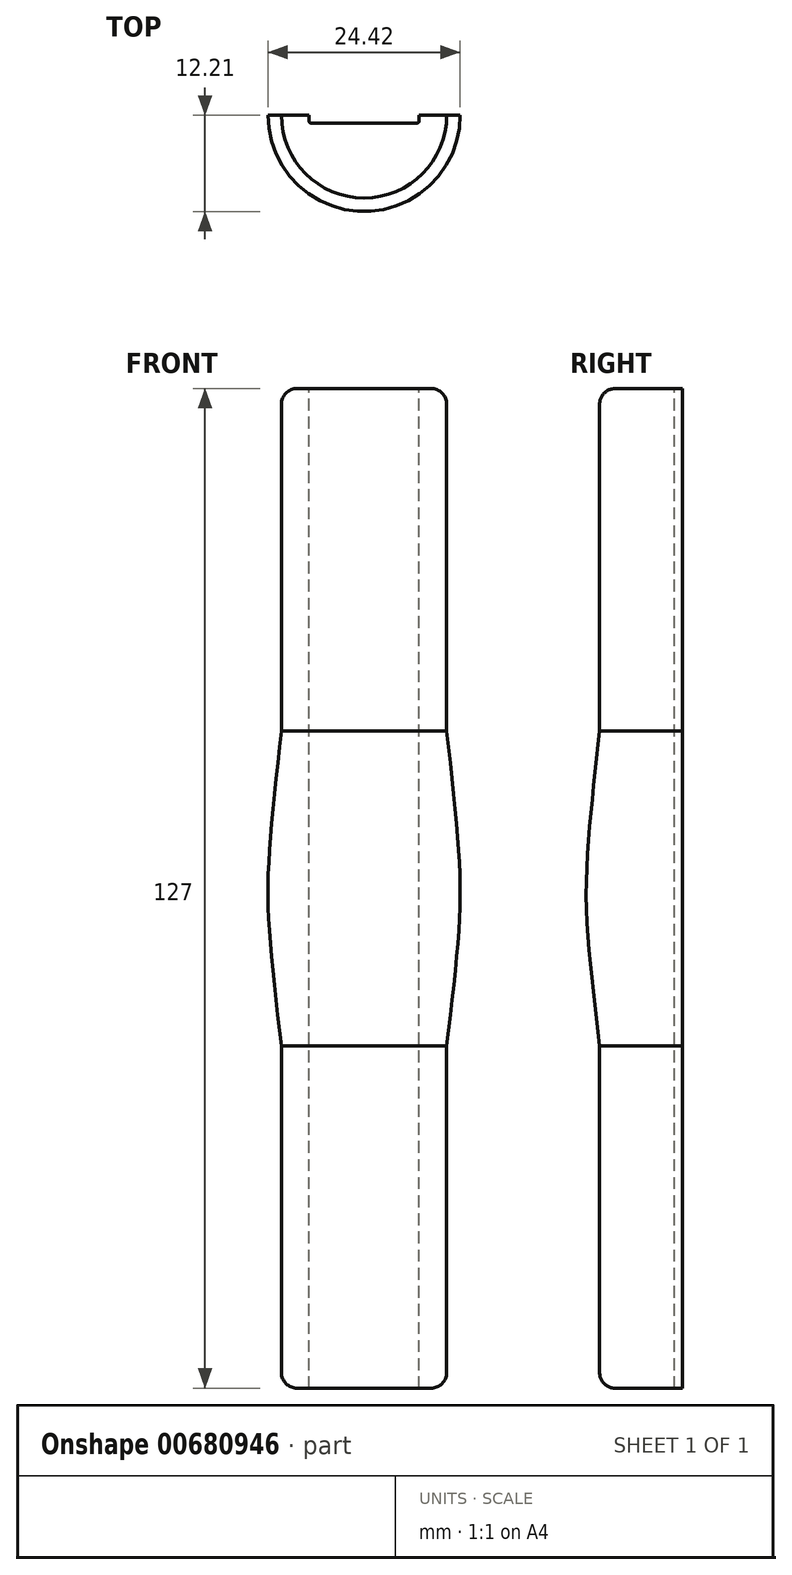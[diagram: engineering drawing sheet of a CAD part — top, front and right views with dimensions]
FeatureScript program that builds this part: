
annotation { "Feature Type Name" : "Feature", "Feature Type Description" : "" }
export const myFeature = defineFeature(function(context is Context, id is Id, definition is map)
    precondition{}
    {
        {
            var Q0;
            Q0=qCreatedBy(makeId("Front.planeOp"),FACE);
            var sketch = newSketch(context, id + "F0", { "sketchPlane" : qUnion([Q0])});
            skLineSegment(sketch, "E0.bottom", {"start": v(-5.25, 63.5) * mm, "end": v(5.25, 63.5) * mm});
            skLineSegment(sketch, "E0.top", {"start": v(-5.25, -63.5) * mm, "end": v(5.25, -63.5) * mm});
            skLineSegment(sketch, "E0.left", {"start": v(-5.25, 63.5) * mm, "end": v(-5.25, 20) * mm});
            skLineSegment(sketch, "E0.right", {"start": v(5.25, 63.5) * mm, "end": v(5.25, -63.5) * mm});
            skPoint(sketch, "E0.middle", {"position": v(0, 0) * mm});
            skFitSpline(sketch, "E1", {"points": [v(-5.25, 20) * mm, v(-6.8, 4.2) * mm, v(-6.8, -5.12) * mm, v(-5.25, -20) * mm], "startDerivative": vector(-5.22, -46.75) * mm, "endDerivative": vector(5.38, -45.13) * mm});
            skLineSegment(sketch, "E2.trimOffspring", {"start": v(-5.25, -20) * mm, "end": v(-5.25, -63.5) * mm});
            skPoint(sketch, "E3.orphan", {"position": v(-5.25, 0) * mm});
            skSolve(sketch);
        }
        {
            var Q0;
            Q0=makeQuery(id+"F0.imprint","IMPRINT",FACE,{"disambiguationData":[TD([[makeQuery(id+"F0.imprint","IMPRINT",EDGE,{"derivedFrom":sQuery(id+"F0.wireOp",EDGE,"E0.bottom")}),-1.0]])]});
            var Q1;
            Q1=sQuery(id+"F0.wireOp",EDGE,"E0.right");
            revolve(context, id + "F1", {"entities" : qUnion([Q0]), "axis" : qUnion([Q1]), "revolveType" : RevolveType.ONE_DIRECTION, "angle" : 180 * degree});
        }
        {
            var Q0;
            Q0=makeQuery(id+"F1.opRevolve","SWEPT_FACE",FACE,{"disambiguationData":[OSD([sQuery(id+"F0.wireOp",EDGE,"E0.bottom")])]});
            var sketch = newSketch(context, id + "F2", { "sketchPlane" : qUnion([Q0])});
            skLineSegment(sketch, "E4", {"start": v(5.25, 0) * mm, "end": v(-1.75, 0) * mm});
            skLineSegment(sketch, "E5", {"start": v(5.25, 0) * mm, "end": v(12.25, 0) * mm});
            skLineSegment(sketch, "E6", {"start": v(12.25, 0) * mm, "end": v(12.25, 0.7) * mm});
            skLineSegment(sketch, "E7", {"start": v(11.95, 1) * mm, "end": v(-1.45, 1) * mm});
            skLineSegment(sketch, "E8", {"start": v(-1.75, 0.7) * mm, "end": v(-1.75, 0) * mm});
            skPoint(sketch, "E9.visualSharp", {"position": v(-1.75, 1) * mm});
            skArc(sketch, "E9.filletArc", {"start": v(-1.45, 1) * mm, "mid": v(-1.66, 0.91) * mm, "end": v(-1.75, 0.7) * mm});
            skPoint(sketch, "E10.visualSharp", {"position": v(12.25, 1) * mm});
            skArc(sketch, "E10.filletArc", {"start": v(12.25, 0.7) * mm, "mid": v(12.16, 0.91) * mm, "end": v(11.95, 1) * mm});
            skSolve(sketch);
        }
        {
            var Q0;
            Q0=makeQuery(id+"F2.imprint","IMPRINT",FACE,{"disambiguationData":[TD([[makeQuery(id+"F2.imprint","IMPRINT",EDGE,{"derivedFrom":sQuery(id+"F2.wireOp",EDGE,"E4")}),-1.0]])]});
            extrude(context, id + "F3", {"entities" : qUnion([Q0]), "operationType" : NewBodyOperationType.REMOVE, "oppositeDirection" : true, "depth" : 127 * mm, "offsetDistance" : 25 * mm});
        }
        {
            var Q0;
            Q0=makeQuery(id+"F1.opRevolve","SWEPT_BODY",BODY,{"disambiguationData":[OSD([sQuery(id+"F0.wireOp",EDGE,"E0.bottom"),sQuery(id+"F0.wireOp",EDGE,"E0.top"),sQuery(id+"F0.wireOp",EDGE,"E0.right"),sQuery(id+"F0.wireOp",EDGE,"E0.left"),sQuery(id+"F0.wireOp",EDGE,"E1"),sQuery(id+"F0.wireOp",EDGE,"E2.trimOffspring")])]});
            var Q1;
            Q1=qCreatedBy(makeId("Front.planeOp"),FACE);
            mirror(context, id + "F4", {"entities" : qUnion([Q0]), "mirrorPlane" : qUnion([Q1])});
        }
        {
            var Q0;
            Q0=makeQuery(id+"F1.opRevolve","SWEPT_BODY",BODY,{"disambiguationData":[OSD([sQuery(id+"F0.wireOp",EDGE,"E0.bottom"),sQuery(id+"F0.wireOp",EDGE,"E0.top"),sQuery(id+"F0.wireOp",EDGE,"E0.right"),sQuery(id+"F0.wireOp",EDGE,"E0.left"),sQuery(id+"F0.wireOp",EDGE,"E1"),sQuery(id+"F0.wireOp",EDGE,"E2.trimOffspring")])]});
            deleteBodies(context, id + "F5", {"entities" : qUnion([Q0])});
        }
        {
            var Q0;
            Q0=makeQuery(id+"F4.opPattern","COPY",EDGE,{"derivedFrom":makeQuery(id+"F1.opRevolve","SWEPT_EDGE",EDGE,{"disambiguationData":[OSD([sQuery(id+"F0.wireOp",EDGE,"E0.bottom"),sQuery(id+"F0.wireOp",EDGE,"E0.left")])]}),"instanceName":"1"});
            fillet(context, id + "F6", {"entities" : qUnion([Q0]), "radius" : 2 * mm, "tangentPropagation" : true, "allowEdgeOverflow" : false});
        }
        {
            var Q0;
            Q0=makeQuery(id+"F4.opPattern","COPY",EDGE,{"derivedFrom":makeQuery(id+"F1.opRevolve","SWEPT_EDGE",EDGE,{"disambiguationData":[OSD([sQuery(id+"F0.wireOp",EDGE,"E0.top"),sQuery(id+"F0.wireOp",EDGE,"E2.trimOffspring")])]}),"instanceName":"1"});
            fillet(context, id + "F7", {"entities" : qUnion([Q0]), "radius" : 2 * mm, "tangentPropagation" : true, "allowEdgeOverflow" : false});
        }
    });
